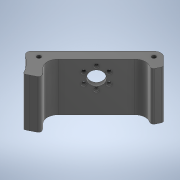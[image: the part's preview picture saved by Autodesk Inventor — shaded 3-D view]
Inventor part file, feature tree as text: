
AUTODESK INVENTOR PART (.ipt)
format: ipt  version: 2020 (Build 240168000, 168)  size: 397,312 bytes
history: native  units: mm
features: extrude x4, sketch x3, other x1, chamfer x1, fillet x1
ambient origin geometry x8: Origin, YZ Plane, XZ Plane, XY Plane, X Axis, Y Axis, Z Axis, Center Point
bodies: Body1 (feature_tree)
feature tree (10):
  other  "Твердое тело1"
  sketch  "Эскиз1"
  extrude  "Выдавливание10"  Depth=2.9mm
  sketch  "Эскиз6"
  extrude  "Выдавливание13"  Depth=6.0mm
  extrude  "Выдавливание14"  Depth=35.0mm TaperAngle=0.0deg
  chamfer  "Фаска3"  Distance=59.0mm
  extrude  "Выдавливание15"  Depth=21.0mm
  fillet  "Сопряжение1"  Radius=15.0mm
  sketch  "Эскиз7"
